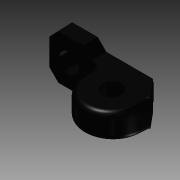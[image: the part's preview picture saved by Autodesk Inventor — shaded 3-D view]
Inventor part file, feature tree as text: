
AUTODESK INVENTOR PART (.ipt)
format: ipt  version: 2015 SP1 (Build 190203100, 203)  size: 413,184 bytes
history: native  units: in
note: dims shown in document units (in); Inventor stores cm internally (conversion verified against a paired STEP export)
features: other x2, extrude x2, sketch x2, imported_body x1
ambient origin geometry x8: Origin, YZ Plane, XZ Plane, XY Plane, X Axis, Y Axis, Z Axis, Center Point
bodies: Body1 (feature_tree)
feature tree (7):
  parser-record x1  (decoder bookkeeping rows leaked as tree rows — omitted from the tree; the rows remain in map.json)
  other  "Pillow Block"
  extrude  "Extrusion1"  TaperAngle=0.0deg  [1 undecoded]
  extrude  "Extrusion2"  Depth=1.0in
  imported_body  "Base1"
  sketch  "Sketch1"  dims[d2=0.0in d3=0.0in]
  sketch  "Sketch2"  dims[d4=0.0in d6=0.3436in d7=1.0in d8=0.0in d9=0.1in d10=1.0in d11=0.0in d12=0.02in]
note: 1 required parameter value undecoded (feature->parameter linkage not recoverable at this tier; creation-order binding heuristic only, values carry confidence <= 0.55)
